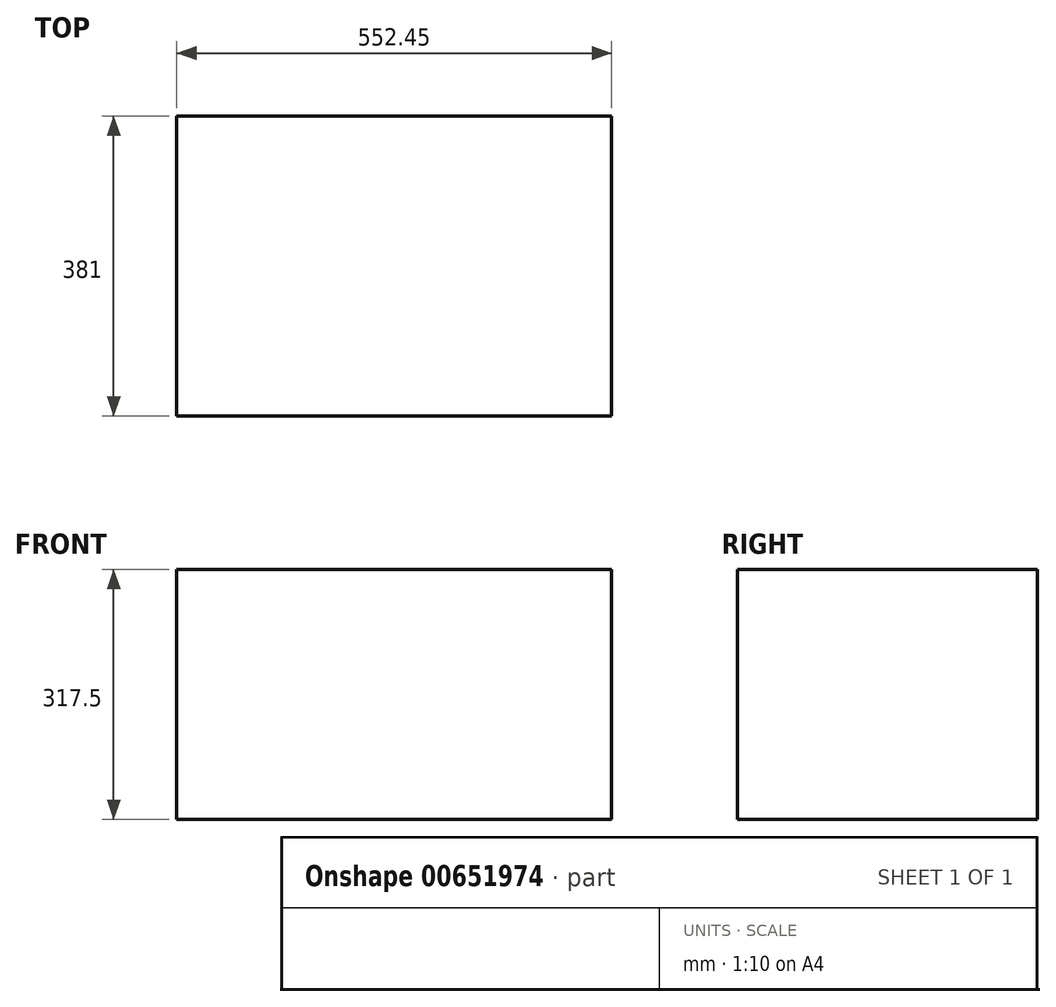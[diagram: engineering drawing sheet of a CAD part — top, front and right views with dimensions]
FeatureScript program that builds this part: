
annotation { "Feature Type Name" : "Feature", "Feature Type Description" : "" }
export const myFeature = defineFeature(function(context is Context, id is Id, definition is map)
    precondition{}
    {
        {
            var Q0;
            Q0=qCreatedBy(makeId("Top.planeOp"),FACE);
            var sketch = newSketch(context, id + "F0", { "sketchPlane" : qUnion([Q0])});
            skLineSegment(sketch, "E0.bottom", {"start": v(0, 0) * mm, "end": v(552.45, 0) * mm});
            skLineSegment(sketch, "E0.top", {"start": v(0, 381) * mm, "end": v(552.45, 381) * mm});
            skLineSegment(sketch, "E0.left", {"start": v(0, 0) * mm, "end": v(0, 381) * mm});
            skLineSegment(sketch, "E0.right", {"start": v(552.45, 0) * mm, "end": v(552.45, 381) * mm});
            skSolve(sketch);
        }
        {
            var Q0;
            Q0=makeQuery(id+"F0.imprint","IMPRINT",FACE,{"disambiguationData":[TD([[makeQuery(id+"F0.imprint","IMPRINT",EDGE,{"derivedFrom":sQuery(id+"F0.wireOp",EDGE,"E0.bottom")}),1.0]])]});
            extrude(context, id + "F1", {"entities" : qUnion([Q0]), "depth" : 317.5 * mm, "offsetDistance" : 25.4 * mm});
        }
    });
